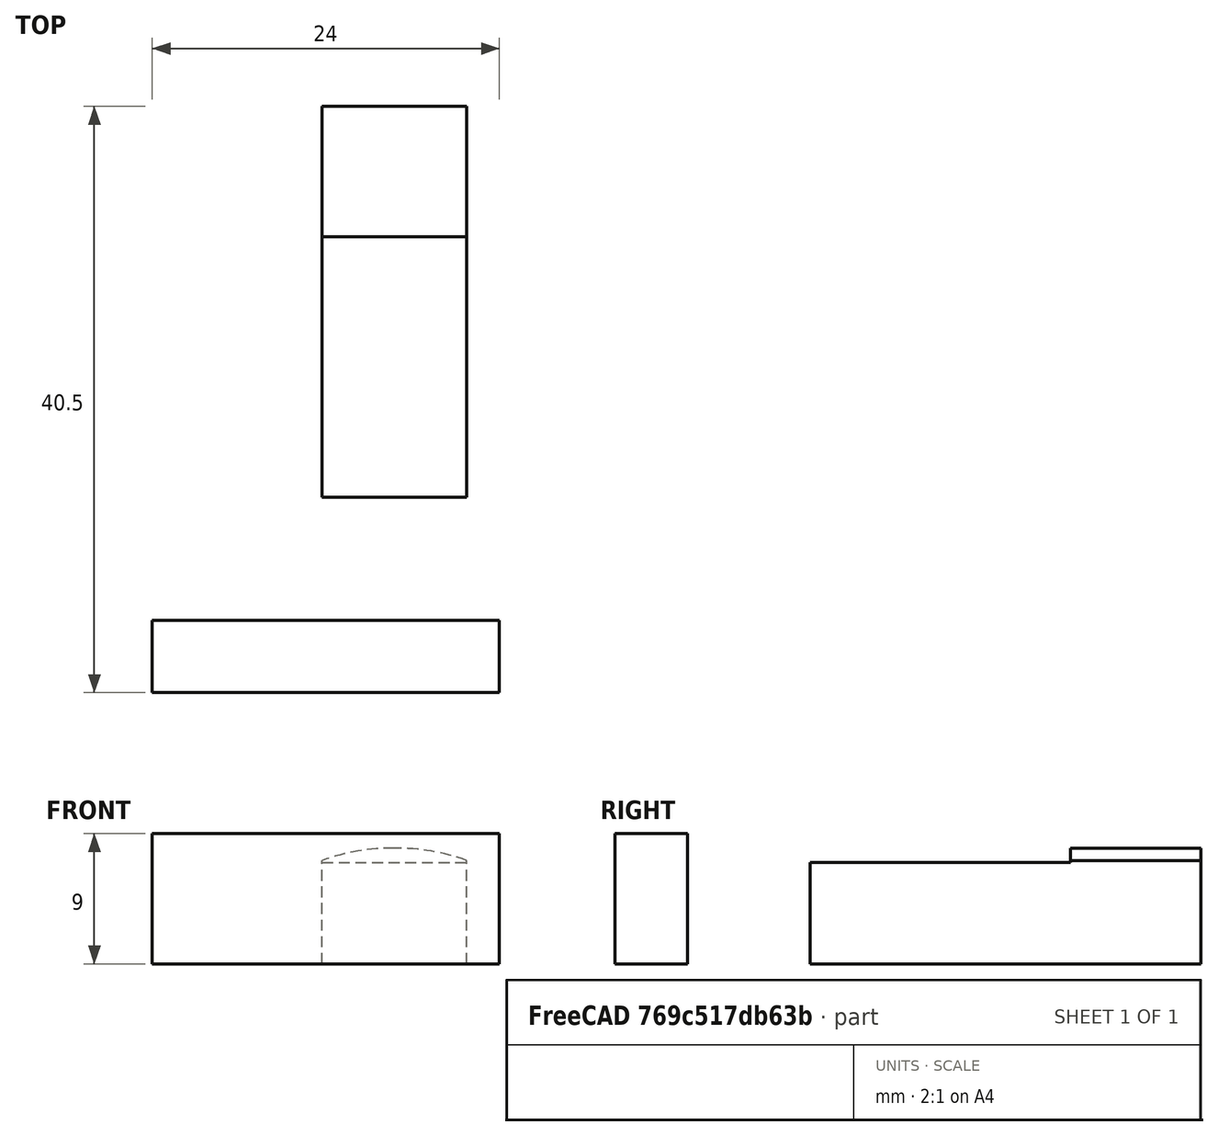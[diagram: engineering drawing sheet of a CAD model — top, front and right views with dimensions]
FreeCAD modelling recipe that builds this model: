
FCSTD DOCUMENT  (FreeCAD 0.16R4924 (Git))
Label: pin_v3p1
License: All rights reserved
LicenseURL: http://en.wikipedia.org/wiki/All_rights_reserved
objects: Part::Feature×12, Part::Box×3, App::MeasureDistance×2, Part::Cylinder×1, Part::MultiCommon×1, Part::Cut×1, Part::MultiFuse×1, Part::Fuse×1
note: 20 computed .brp shape members not serialized (recipe doc carries the construction recipe); baked Part::Feature solids carry a one-line shape summary decoded from their .brp

FEATURE [Part::Cylinder] Cylinder  label="rounded_top"
  Angle = 360
  Height = 40
  Placement = pos=(5,35,-7) rot=(1,0,0;1.5708rad)
  Radius = 15
FEATURE [Part::Box] Box  label="pin"
  Height = 8
  Length = 10
  Width = 27
FEATURE [Part::MultiCommon] Common  label="rounded pin"
  Shapes = -> [Cylinder,Box]
FEATURE [Part::Box] Box001  label="flat_top"
  Height = 10
  Length = 10
  Placement = pos=(0,0,7) rot=(0,0,1;0rad)
  Width = 18
FEATURE [Part::Cut] Cut
  Base = -> Common
  Placement = pos=(0,11,0) rot=(0,0,1;0rad)
  Tool = -> Box001
FEATURE [App::MeasureDistance] Distance  label="Distance: 24.786"
  Distance = 24.7864
  P1 = (9.694,0,7)
  P2 = (10,24.7829,6.71956)
FEATURE [App::MeasureDistance] Distance001  label="Distance: 6.780"
  Distance = 6.78023
  P1 = (9.70016,20,7.23869)
  P2 = (9.22289,26.7617,7.39237)
FEATURE [Part::Box] cube
  Height = 5
  Length = 24
  Placement = pos=(-12,-4.5,-2.5) rot=(0,0,1;0rad)
  Width = 9
FEATURE [Part::Feature] polyhedron
  Placement = pos=(-11.2451,0,2.5) rot=(0,0,1;0rad)
  shape: bbox 1.51 x 9 x 1.337 mm, 6 faces (baked)
FEATURE [Part::Feature] polyhedron001
  Placement = pos=(-9.24512,0,2.5) rot=(0,0,1;0rad)
  shape: bbox 1.51 x 9 x 1.337 mm, 6 faces (baked)
FEATURE [Part::Feature] polyhedron002
  Placement = pos=(-7.24512,0,2.5) rot=(0,0,1;0rad)
  shape: bbox 1.51 x 9 x 1.337 mm, 6 faces (baked)
FEATURE [Part::Feature] polyhedron003
  Placement = pos=(-5.24512,0,2.5) rot=(0,0,1;0rad)
  shape: bbox 1.51 x 9 x 1.337 mm, 6 faces (baked)
FEATURE [Part::Feature] polyhedron004
  Placement = pos=(-3.24512,0,2.5) rot=(0,0,1;0rad)
  shape: bbox 1.51 x 9 x 1.337 mm, 6 faces (baked)
FEATURE [Part::Feature] polyhedron005
  Placement = pos=(-1.24512,0,2.5) rot=(0,0,1;0rad)
  shape: bbox 1.51 x 9 x 1.337 mm, 6 faces (baked)
FEATURE [Part::Feature] polyhedron006
  Placement = pos=(0.754882,0,2.5) rot=(0,0,1;0rad)
  shape: bbox 1.51 x 9 x 1.337 mm, 6 faces (baked)
FEATURE [Part::Feature] polyhedron007
  Placement = pos=(2.75488,0,2.5) rot=(0,0,1;0rad)
  shape: bbox 1.51 x 9 x 1.337 mm, 6 faces (baked)
FEATURE [Part::Feature] polyhedron008
  Placement = pos=(4.75488,0,2.5) rot=(0,0,1;0rad)
  shape: bbox 1.51 x 9 x 1.337 mm, 6 faces (baked)
FEATURE [Part::Feature] polyhedron009
  Placement = pos=(6.75488,0,2.5) rot=(0,0,1;0rad)
  shape: bbox 1.51 x 9 x 1.337 mm, 6 faces (baked)
FEATURE [Part::Feature] polyhedron010
  Placement = pos=(8.75488,0,2.5) rot=(0,0,1;0rad)
  shape: bbox 1.51 x 9 x 1.337 mm, 6 faces (baked)
FEATURE [Part::Feature] polyhedron011
  Placement = pos=(10.7549,0,2.5) rot=(0,0,1;0rad)
  shape: bbox 1.51 x 9 x 1.337 mm, 6 faces (baked)
FEATURE [Part::MultiFuse] Group
  Shapes = -> [polyhedron,polyhedron001,polyhedron002,polyhedron003,polyhedron004,polyhedron005,polyhedron006,polyhedron007,polyhedron008,polyhedron009,polyhedron010,polyhedron011]
FEATURE [Part::Fuse] union  label="rack"
  Base = -> cube
  Placement = pos=(0.245118,0,4.5) rot=(1,0,0;1.5708rad)
  Tool = -> Group
